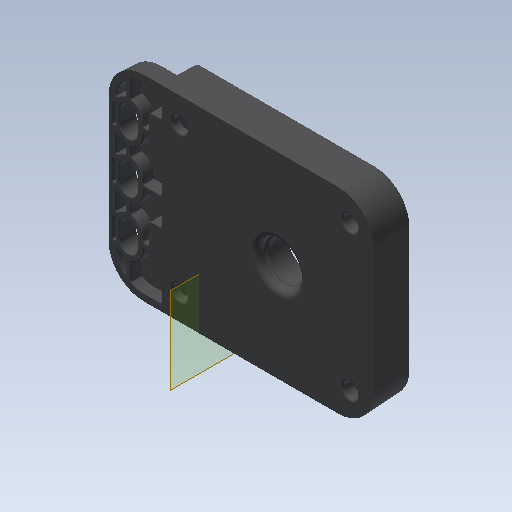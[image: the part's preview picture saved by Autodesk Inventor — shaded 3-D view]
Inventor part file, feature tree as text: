
AUTODESK INVENTOR PART (.ipt)
format: ipt  version: 2020 (Build 240168000, 168)  size: 1,016,320 bytes
history: native  units: mm
features: extrude x19, sketch x15, fillet x11, plane x4, hole x2, projected_geometry x1
ambient origin geometry x8: Origin, YZ Plane, XZ Plane, XY Plane, X Axis, Y Axis, Z Axis, Center Point
bodies: Solid1 (feature_tree)
feature tree (52):
  extrude  "Extrusion1"  TaperAngle=0.0deg  [1 undecoded]
  plane  "Work Plane1"
  extrude  "Extrusion2"  Depth=15.882496mm
  fillet  "Fillet1"  Radius=13.081mm
  plane  "Work Plane2"
  sketch  "Sketch5"  dims[d6=9.4996mm d7=0.0mm d8=-1.4986mm d9=8.9916mm]
  extrude  "Extrusion3"  Depth=8.9916mm
  extrude  "Extrusion4"  Depth=0.6096mm
  sketch  "Sketch9"  dims[d10=8.6614mm d12=0.6096mm d13=0.993147mm]
  sketch  "Sketch10"  dims[d14=0.6096mm d15=0.6096mm]
  extrude  "Extrusion10"  Depth=0.6096mm
  extrude  "Extrusion11"  Depth=7.668253mm
  extrude  "Extrusion12"  Depth=7.054107mm
  extrude  "Extrusion13"  Depth=6.1976mm
  hole  "Hole1"  [1 undecoded]
  plane  "Work Plane3"
  extrude  "Extrusion14"  Depth=1.9558mm TaperAngle=0.0deg
  fillet  "Fillet6"  Radius=1.4986mm
  extrude  "Extrusion15"  Depth=3.81mm
  hole  "Hole2"  [1 undecoded]
  fillet  "Fillet7"  Radius=15.809192mm
  extrude  "Extrusion17"  Depth=1.4986mm TaperAngle=0.0deg
  extrude  "Extrusion20"  Depth=0.508mm TaperAngle=0.0deg
  extrude  "Extrusion21"  Depth=0.508mm
  extrude  "Extrusion22"  Depth=0.508mm
  extrude  "Extrusion23"  Depth=0.508mm
  extrude  "Extrusion24"  Depth=0.508mm TaperAngle=0.0deg
  fillet  "Fillet10"  Radius=1.4986mm
  fillet  "Fillet11"  Radius=13.4874mm
  fillet  "Fillet12"  Radius=6.2484mm
  sketch  "Sketch22"  dims[d66=0.508mm d67=1.4986mm d68=0.0mm]
  extrude  "Extrusion25"  Depth=0.508mm
  extrude  "Extrusion26"  Depth=0.508mm TaperAngle=0.0deg
  fillet  "Fillet13"  Radius=9.4996mm
  fillet  "Fillet14"  Radius=4.5466mm
  fillet  "Fillet15"  Radius=2.159mm
  fillet  "Fillet16"  Radius=1.4986mm
  extrude  "Extrusion27"  Depth=0.508mm
  fillet  "Fillet17"  Radius=0.508mm
  plane  "Work Plane4"
  sketch  "Sketch1"  dims[d0=9.4996mm d1=-0.349066mm d2=0.0mm]
  sketch  "Sketch2"  dims[d3=5.0038mm d4=15.882496mm d5=13.081mm]
  projected_geometry  "Projected Loop1"
  sketch  "Sketch11"  dims[d16=7.054107mm d17=7.668253mm]
  sketch  "Sketch12"  dims[d18=8.668253mm d19=7.054107mm]
  sketch  "Sketch13"  dims[d20=1.4986mm d21=0.0mm d22=6.1976mm d23=-0.087266mm]
  sketch  "Sketch14"  dims[d36=10.6172mm d44=1.9558mm d45=0.0mm]
  sketch  "Sketch18"  dims[d46=1.9558mm d47=0.0mm d48=1.9558mm d49=0.0mm d50=1.4986mm d51=0.0mm]
  sketch  "Sketch19"  dims[d52=2.1082mm d53=19.05mm d54=9.525mm d55=6.35mm d56=14.3117mm d57=25.4mm d58=20.594885mm d59=3.81mm]
  sketch  "Sketch20"  dims[d60=8.6106mm d61=15.809192mm d62=15.809192mm]
  sketch  "Sketch21"  dims[d63=2.6162mm d64=1.4986mm d65=0.0mm]
  sketch  "Sketch23"  dims[d69=6.5024mm d70=18.0594mm d71=6.5024mm d72=3.7846mm d73=19.05mm d74=9.525mm d75=6.35mm d76=14.3117mm d77=25.4mm d78=20.594885mm d79=0.508mm d82=2.9972mm d83=0.0mm d90=1.4986mm d91=0.0mm d92=13.4874mm d93=6.2484mm d94=-0.174533mm d95=10.4902mm d96=4.5466mm d97=0.0mm d98=9.4996mm d99=4.5466mm d100=0.0mm d101=2.159mm d102=0.0mm d103=1.4986mm d104=0.508mm d105=0.508mm d106=25.4mm d107=0.0mm d108=2.6924mm d109=0.0mm d110=0.3048mm d111=0.508mm d112=0.3048mm d113=0.3048mm d114=3.7846mm d115=2.794mm d116=0.0mm d117=0.508mm]
note: 3 required parameter values undecoded (feature->parameter linkage not recoverable at this tier; creation-order binding heuristic only, values carry confidence <= 0.55)
